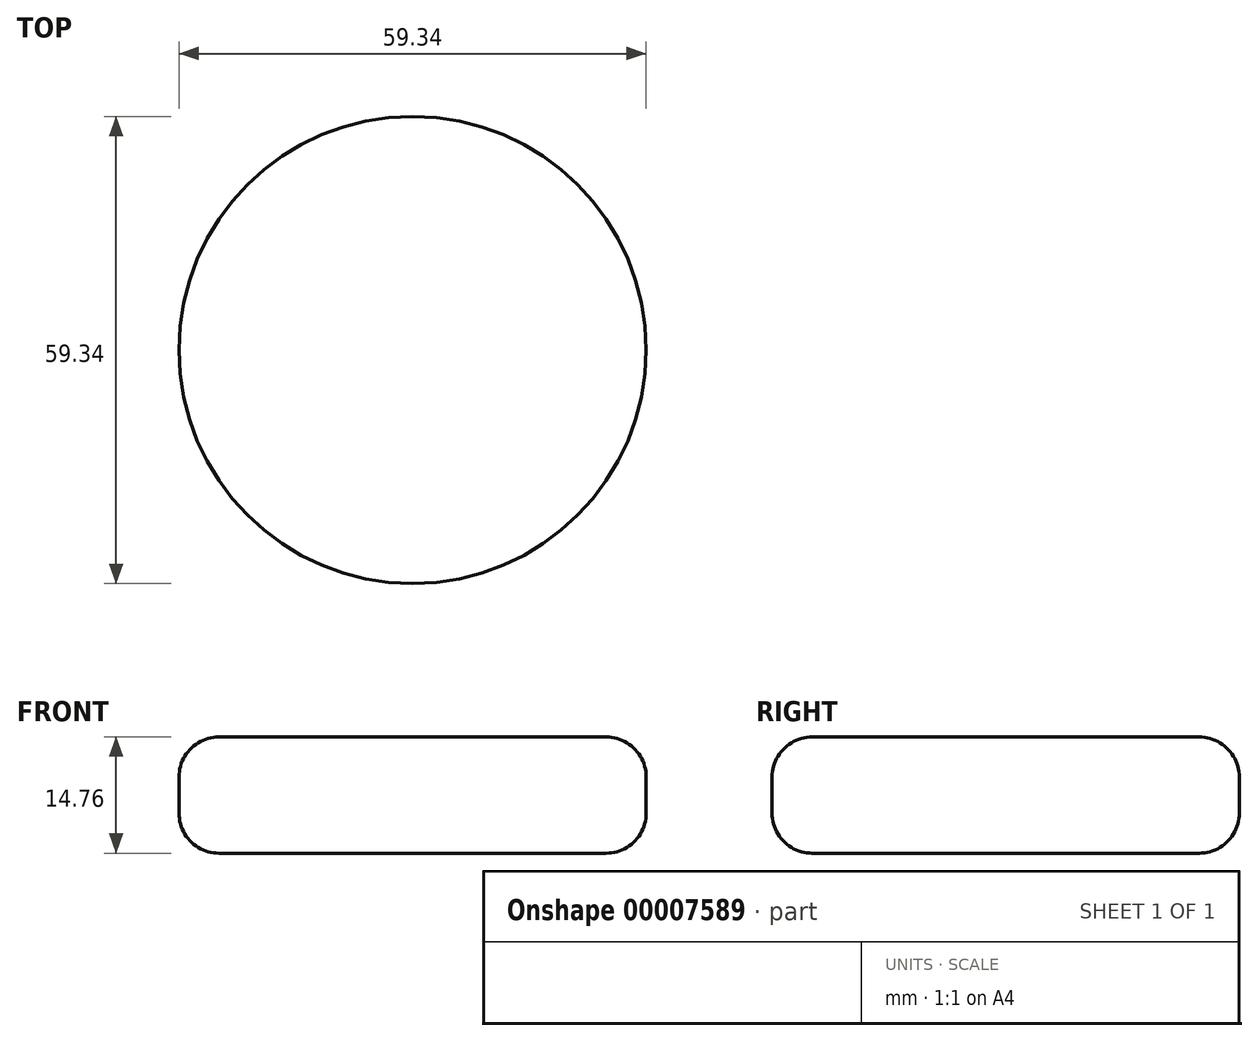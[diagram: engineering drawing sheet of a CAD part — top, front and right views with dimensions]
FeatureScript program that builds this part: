
annotation { "Feature Type Name" : "Feature", "Feature Type Description" : "" }
export const myFeature = defineFeature(function(context is Context, id is Id, definition is map)
    precondition{}
    {
        {
            var Q0;
            Q0=qCreatedBy(makeId("Top.planeOp"),FACE);
            var sketch = newSketch(context, id + "F0", { "sketchPlane" : qUnion([Q0])});
            skCircle(sketch, "E0", {"center": v(0, 0) * mm, "radius": 29.67 * mm});
            skSolve(sketch);
        }
        {
            var Q0;
            Q0 = qSketchRegion(id + "F0", true);
            extrude(context, id + "F1", {"entities" : qUnion([Q0]), "depth" : 14.76 * mm});
        }
        {
            var Q0;
            Q0=makeQuery(id+"F1.opExtrude","SWEPT_FACE",FACE,{"disambiguationData":[OSD([sQuery(id+"F0.wireOp",EDGE,"E0")])]});
            var Q1;
            Q1=makeQuery(id+"F1.opExtrude","CAP_FACE",FACE,{"disambiguationData":[OSD([sQuery(id+"F0.wireOp",EDGE,"E0")])],"isStart":false});
            fillet(context, id + "F2", {"entities" : qUnion([Q0, Q1]), "radius" : 5.08 * mm, "tangentPropagation" : true, "allowEdgeOverflow" : false});
        }
    });
